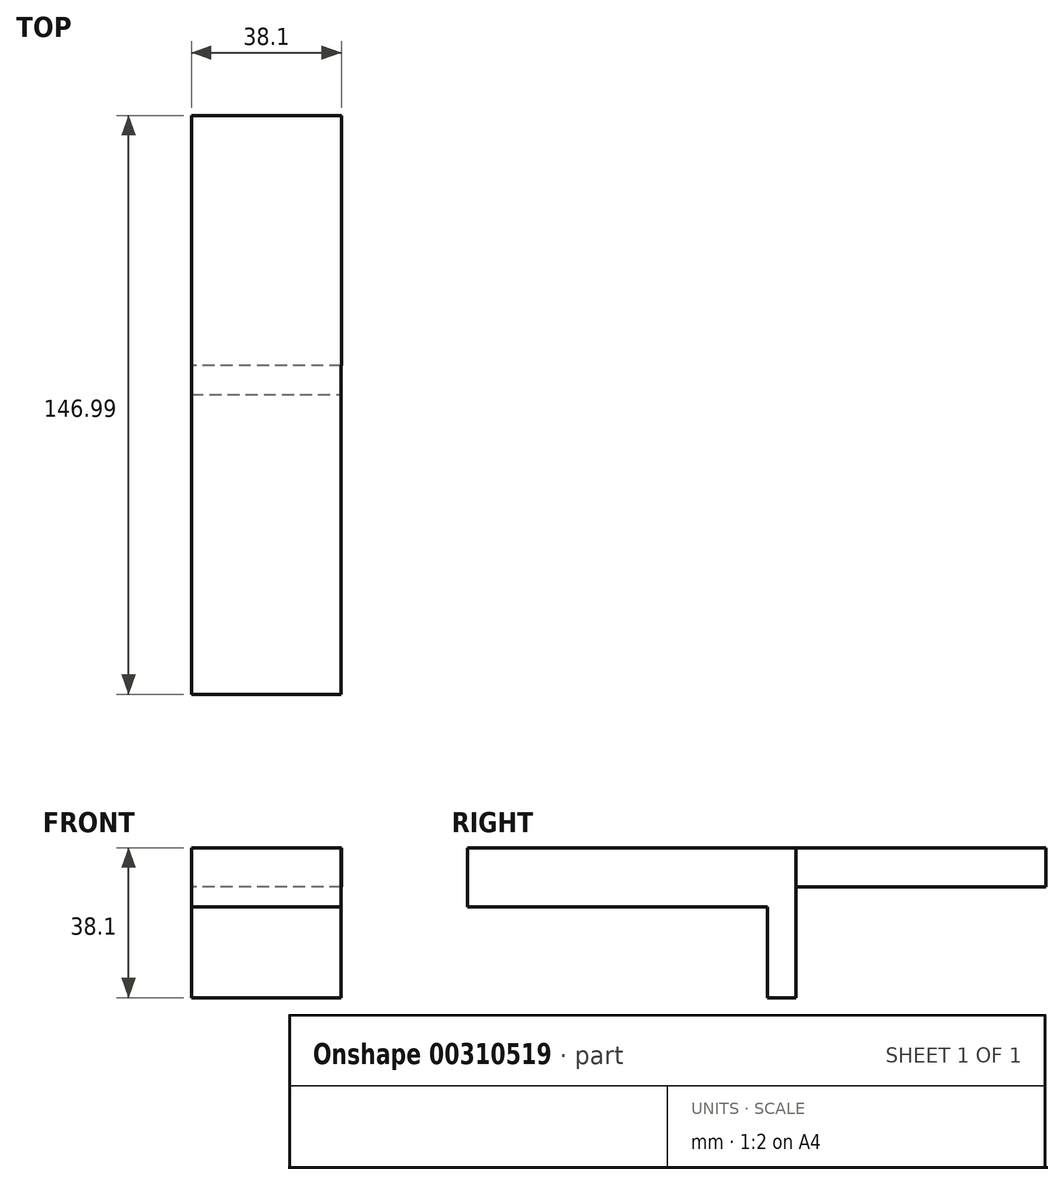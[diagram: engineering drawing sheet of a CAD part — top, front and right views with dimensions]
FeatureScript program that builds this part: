
annotation { "Feature Type Name" : "Feature", "Feature Type Description" : "" }
export const myFeature = defineFeature(function(context is Context, id is Id, definition is map)
    precondition{}
    {
        {
            var Q0;
            Q0=qCreatedBy(makeId("Front.planeOp"),FACE);
            var sketch = newSketch(context, id + "F0", { "sketchPlane" : qUnion([Q0])});
            skLineSegment(sketch, "E0.bottom", {"start": v(19.05, 5) * mm, "end": v(-19.05, 5) * mm});
            skLineSegment(sketch, "E0.top", {"start": v(19.05, -5) * mm, "end": v(-19.05, -5) * mm});
            skLineSegment(sketch, "E0.left", {"start": v(19.05, 5) * mm, "end": v(19.05, -5) * mm});
            skLineSegment(sketch, "E0.right", {"start": v(-19.05, 5) * mm, "end": v(-19.05, -5) * mm});
            skPoint(sketch, "E0.middle", {"position": v(0, 0) * mm});
            skSolve(sketch);
        }
        {
            var Q0;
            Q0=makeQuery(id+"F0.imprint","IMPRINT",FACE,{"disambiguationData":[TD([[makeQuery(id+"F0.imprint","IMPRINT",EDGE,{"derivedFrom":sQuery(id+"F0.wireOp",EDGE,"E0.bottom")}),1.0]])]});
            extrude(context, id + "F1", {"entities" : qUnion([Q0]), "oppositeDirection" : true, "depth" : 63.5 * mm});
        }
        {
            var Q0;
            Q0=makeQuery(id+"F1.opExtrude","SWEPT_FACE",FACE,{"disambiguationData":[OSD([sQuery(id+"F0.wireOp",EDGE,"E0.bottom")])]});
            var sketch = newSketch(context, id + "F2", { "sketchPlane" : qUnion([Q0])});
            skLineSegment(sketch, "E1.bottom", {"start": v(-19.05, 0) * mm, "end": v(19, 0) * mm});
            skLineSegment(sketch, "E1.top", {"start": v(-19.05, -7.3) * mm, "end": v(19, -7.3) * mm});
            skLineSegment(sketch, "E1.left", {"start": v(-19.05, 0) * mm, "end": v(-19.05, -7.3) * mm});
            skLineSegment(sketch, "E1.right", {"start": v(19, 0) * mm, "end": v(19, -7.3) * mm});
            skSolve(sketch);
        }
        {
            var Q0;
            Q0=makeQuery(id+"F2.imprint","IMPRINT",FACE,{"disambiguationData":[TD([[makeQuery(id+"F2.imprint","IMPRINT",EDGE,{"derivedFrom":sQuery(id+"F2.wireOp",EDGE,"E1.bottom")}),1.0]])]});
            extrude(context, id + "F3", {"entities" : qUnion([Q0]), "operationType" : NewBodyOperationType.ADD, "oppositeDirection" : true, "depth" : 38.1 * mm});
        }
        {
            var Q0;
            Q0=makeQuery(id+"F3.opExtrude","SWEPT_FACE",FACE,{"disambiguationData":[OSD([sQuery(id+"F2.wireOp",EDGE,"E1.top")])]});
            var sketch = newSketch(context, id + "F4", { "sketchPlane" : qUnion([Q0])});
            skLineSegment(sketch, "E2.bottom", {"start": v(-19.05, 5) * mm, "end": v(19, 5) * mm});
            skLineSegment(sketch, "E2.top", {"start": v(-19.05, -10) * mm, "end": v(19, -10) * mm});
            skLineSegment(sketch, "E2.left", {"start": v(-19.05, 5) * mm, "end": v(-19.05, -10) * mm});
            skLineSegment(sketch, "E2.right", {"start": v(19, 5) * mm, "end": v(19, -10) * mm});
            skSolve(sketch);
        }
        {
            var Q0;
            Q0 = qSketchRegion(id + "F4", true);
            extrude(context, id + "F5", {"entities" : qUnion([Q0]), "operationType" : NewBodyOperationType.ADD, "depth" : 76.2 * mm});
        }
    });
